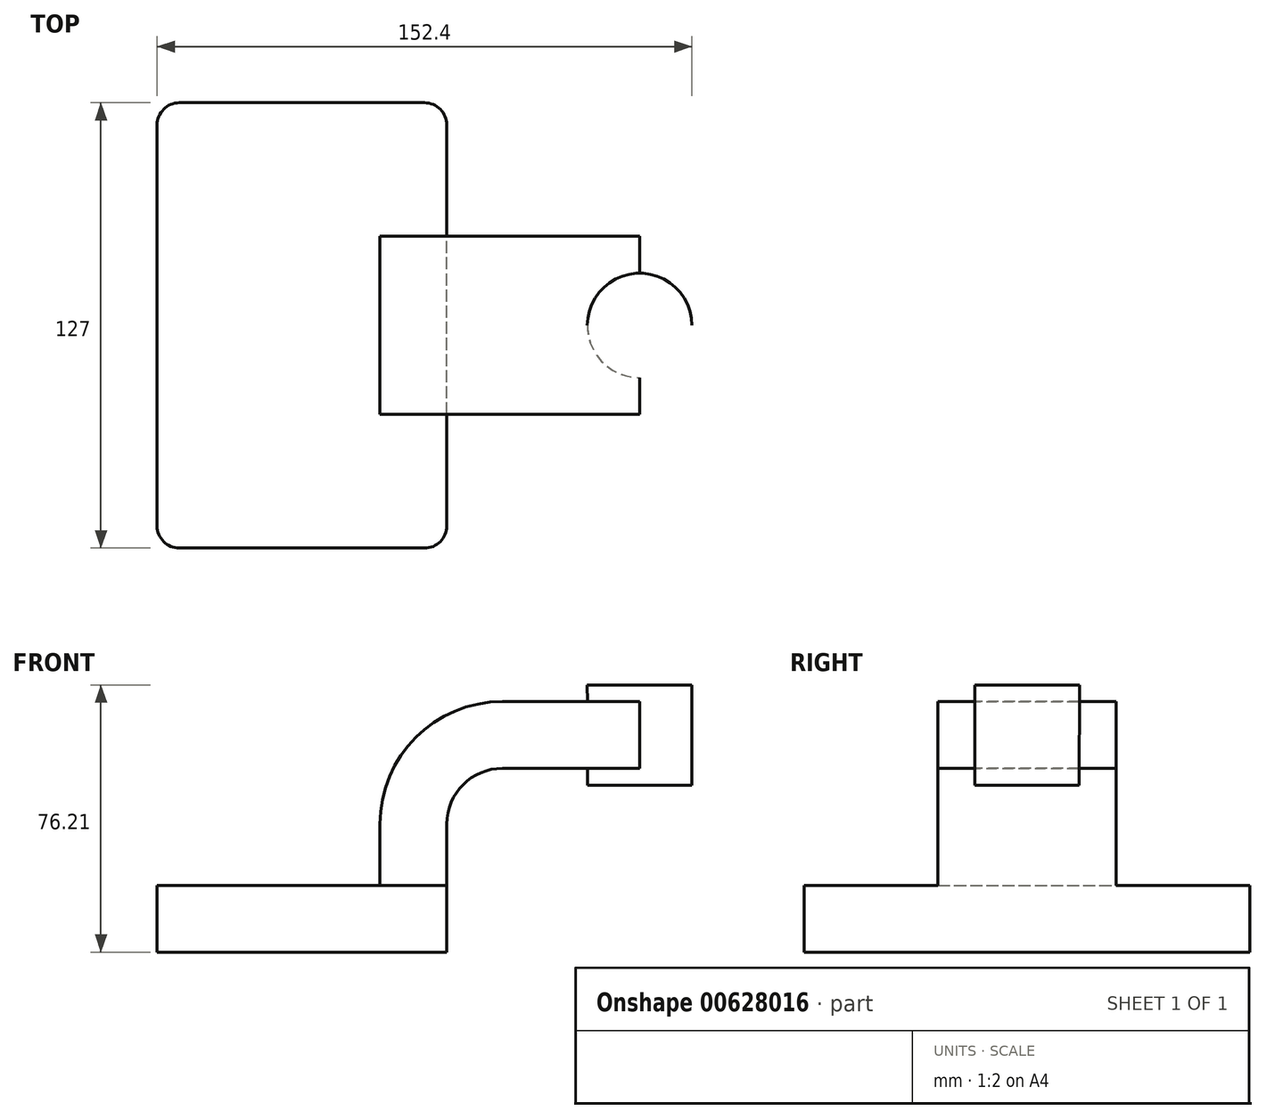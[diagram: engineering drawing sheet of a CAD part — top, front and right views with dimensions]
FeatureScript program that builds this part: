
annotation { "Feature Type Name" : "Feature", "Feature Type Description" : "" }
export const myFeature = defineFeature(function(context is Context, id is Id, definition is map)
    precondition{}
    {
        {
            var Q0;
            Q0=qCreatedBy(makeId("Front.planeOp"),FACE);
            var sketch = newSketch(context, id + "F0", { "sketchPlane" : qUnion([Q0])});
            skLineSegment(sketch, "E0.bottom", {"start": v(41.27, 9.53) * mm, "end": v(-41.28, 9.53) * mm});
            skLineSegment(sketch, "E0.top", {"start": v(41.28, -9.52) * mm, "end": v(-41.27, -9.52) * mm});
            skLineSegment(sketch, "E0.left", {"start": v(41.28, 9.53) * mm, "end": v(41.28, -9.52) * mm});
            skLineSegment(sketch, "E0.right", {"start": v(-41.28, 9.53) * mm, "end": v(-41.27, -9.52) * mm});
            skPoint(sketch, "E0.middle", {"position": v(0, 0) * mm});
            skLineSegment(sketch, "E1.bottom", {"start": v(111.13, 66.68) * mm, "end": v(60.33, 66.68) * mm});
            skLineSegment(sketch, "E1.top", {"start": v(111.13, 38.1) * mm, "end": v(60.33, 38.1) * mm});
            skLineSegment(sketch, "E1.left", {"start": v(111.13, 66.68) * mm, "end": v(111.13, 38.1) * mm});
            skLineSegment(sketch, "E1.right", {"start": v(60.33, 66.68) * mm, "end": v(60.33, 38.1) * mm});
            skPoint(sketch, "E1.middle", {"position": v(85.73, 52.39) * mm});
            skLineSegment(sketch, "E2", {"start": v(41.27, 9.53) * mm, "end": v(41.27, 27) * mm});
            skArc(sketch, "E3", {"start": v(41.27, 27) * mm, "mid": v(45.92, 38.23) * mm, "end": v(57.15, 42.88) * mm});
            skLineSegment(sketch, "E4", {"start": v(57.15, 42.88) * mm, "end": v(96.23, 42.88) * mm});
            skLineSegment(sketch, "E5.0", {"start": v(57.15, 61.93) * mm, "end": v(96.23, 61.93) * mm});
            skArc(sketch, "E5.1", {"start": v(22.23, 27) * mm, "mid": v(32.45, 51.7) * mm, "end": v(57.15, 61.93) * mm});
            skLineSegment(sketch, "E5.2", {"start": v(22.23, 9.53) * mm, "end": v(22.23, 27) * mm});
            skLineSegment(sketch, "E6", {"start": v(96.22, 66.68) * mm, "end": v(96.23, 38.1) * mm});
            skFitSpline(sketch, "E7", {"points": [v(-41.28, 9.53) * mm, v(60.33, 61.93) * mm], "startDerivative": vector(2.17, 112.96) * mm, "endDerivative": vector(125.3, -11.79) * mm});
            skSolve(sketch);
        }
        {
            var Q0;
            Q0=makeQuery(id+"F0.imprint","IMPRINT",FACE,{"disambiguationData":[TD([[makeQuery(id+"F0.imprint","IMPRINT",EDGE,{"derivedFrom":sQuery(id+"F0.wireOp",EDGE,"E0.top")}),-1.0]])]});
            extrude(context, id + "F1", {"entities" : qUnion([Q0]), "endBound" : BoundingType.SYMMETRIC, "depth" : 127 * mm, "offsetDistance" : 25.4 * mm});
        }
        {
            var Q0;
            {var subQ1=sQuery(id+"F0.wireOp",EDGE,"E2");Q0=makeQuery(id+"F0.imprint","IMPRINT",FACE,{"disambiguationData":[TD([[makeQuery(id+"F0.imprint","IMPRINT",EDGE,{"derivedFrom":subQ1}),1.0]])]});}
            var Q1;
            {var subQ1=sQuery(id+"F0.wireOp",EDGE,"E1.right");var subQ3=sQuery(id+"F0.wireOp",EDGE,"E4");var subQ4=makeQuery(id+"F0.imprint","INTERSECT",VERTEX,{"derivedFrom":[subQ1,subQ3]});Q1=makeQuery(id+"F0.imprint","IMPRINT",FACE,{"disambiguationData":[TD([[makeQuery(id+"F0.imprint","IMPRINT",EDGE,{"disambiguationData":[TD([[subQ4,-1.0]])],"derivedFrom":subQ3}),1.0]])]});}
            extrude(context, id + "F2", {"entities" : qUnion([Q0, Q1]), "operationType" : NewBodyOperationType.ADD, "endBound" : BoundingType.SYMMETRIC, "depth" : 50.8 * mm, "offsetDistance" : 25.4 * mm});
        }
        {
            var Q0;
            {var subQ1=sQuery(id+"F0.wireOp",EDGE,"E5.1");Q0=makeQuery(id+"F0.imprint","IMPRINT",FACE,{"disambiguationData":[TD([[makeQuery(id+"F0.imprint","IMPRINT",EDGE,{"derivedFrom":subQ1}),1.0]])]});}
            extrude(context, id + "F3", {"entities" : qUnion([Q0]), "operationType" : NewBodyOperationType.ADD, "depth" : 15.88 * mm, "offsetDistance" : 25.4 * mm});
        }
        {
            var Q0;
            {var subQ4=sQuery(id+"F0.wireOp",EDGE,"E1.left");Q0=makeQuery(id+"F0.imprint","IMPRINT",FACE,{"disambiguationData":[TD([[makeQuery(id+"F0.imprint","IMPRINT",EDGE,{"derivedFrom":subQ4}),-1.0]])]});}
            var Q1;
            Q1=sQuery(id+"F0.wireOp",EDGE,"E6");
            revolve(context, id + "F4", {"operationType" : NewBodyOperationType.ADD, "entities" : qUnion([Q0]), "axis" : qUnion([Q1]), "revolveType" : RevolveType.FULL});
        }
        {
            var Q0;
            Q0=makeQuery(id+"F1.opExtrude","CAP_EDGE",EDGE,{"disambiguationData":[OSD([sQuery(id+"F0.wireOp",EDGE,"E0.left")])],"isStart":false});
            var Q1;
            Q1=makeQuery(id+"F1.opExtrude","CAP_EDGE",EDGE,{"disambiguationData":[OSD([sQuery(id+"F0.wireOp",EDGE,"E0.right")])],"isStart":false});
            var Q2;
            Q2=makeQuery(id+"F1.opExtrude","CAP_EDGE",EDGE,{"disambiguationData":[OSD([sQuery(id+"F0.wireOp",EDGE,"E0.right")])],"isStart":true});
            var Q3;
            Q3=makeQuery(id+"F1.opExtrude","CAP_EDGE",EDGE,{"disambiguationData":[OSD([sQuery(id+"F0.wireOp",EDGE,"E0.left")])],"isStart":true});
            fillet(context, id + "F5", {"entities" : qUnion([Q0, Q1, Q2, Q3]), "radius" : 6.35 * mm, "tangentPropagation" : true, "allowEdgeOverflow" : false});
        }
    });
